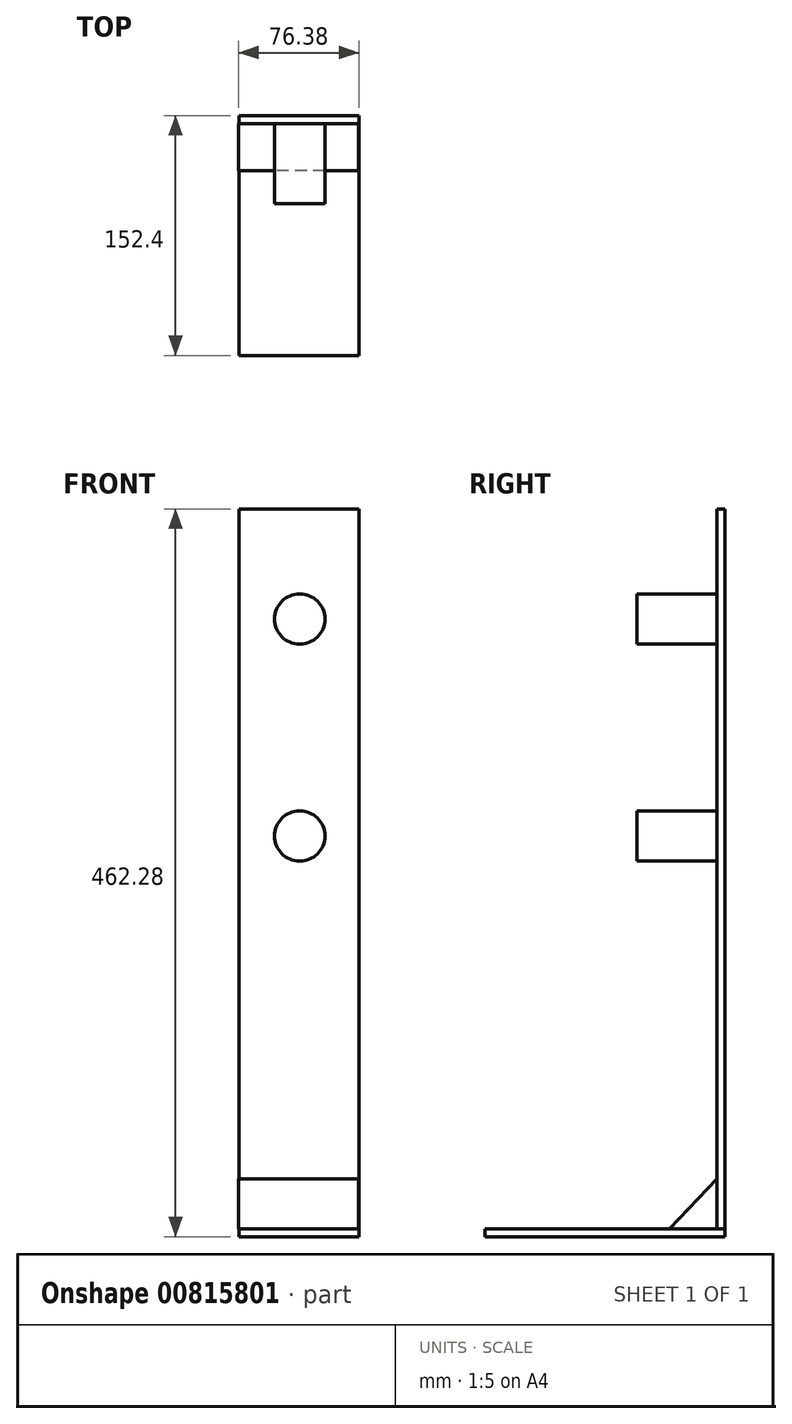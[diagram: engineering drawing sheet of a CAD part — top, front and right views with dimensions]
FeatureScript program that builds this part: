
annotation { "Feature Type Name" : "Feature", "Feature Type Description" : "" }
export const myFeature = defineFeature(function(context is Context, id is Id, definition is map)
    precondition{}
    {
        {
            var Q0;
            Q0=qCreatedBy(makeId("Top.planeOp"),FACE);
            var sketch = newSketch(context, id + "F0", { "sketchPlane" : qUnion([Q0])});
            skLineSegment(sketch, "E0.bottom", {"start": v(-25.22, 0) * mm, "end": v(50.98, 0) * mm});
            skLineSegment(sketch, "E0.top", {"start": v(-25.22, -152.4) * mm, "end": v(50.98, -152.4) * mm});
            skLineSegment(sketch, "E0.left", {"start": v(-25.22, 0) * mm, "end": v(-25.22, -152.4) * mm});
            skLineSegment(sketch, "E0.right", {"start": v(50.98, 0) * mm, "end": v(50.98, -152.4) * mm});
            skSolve(sketch);
        }
        {
            var Q0;
            Q0 = qSketchRegion(id + "F0", true);
            extrude(context, id + "F1", {"entities" : qUnion([Q0]), "depth" : 5.08 * mm, "offsetDistance" : 25.4 * mm});
        }
        {
            var Q0;
            Q0=qCreatedBy(makeId("Front.planeOp"),FACE);
            var sketch = newSketch(context, id + "F2", { "sketchPlane" : qUnion([Q0])});
            skLineSegment(sketch, "E1.bottom", {"start": v(50.98, 5.08) * mm, "end": v(-25.22, 5.08) * mm});
            skLineSegment(sketch, "E1.top", {"start": v(50.98, 462.28) * mm, "end": v(-25.22, 462.28) * mm});
            skLineSegment(sketch, "E1.left", {"start": v(50.98, 5.08) * mm, "end": v(50.98, 462.28) * mm});
            skLineSegment(sketch, "E1.right", {"start": v(-25.22, 5.08) * mm, "end": v(-25.22, 462.28) * mm});
            skPoint(sketch, "E1.middle", {"position": v(-63.32, 233.68) * mm});
            skSolve(sketch);
        }
        {
            var Q0;
            Q0 = qSketchRegion(id + "F2", true);
            extrude(context, id + "F3", {"entities" : qUnion([Q0]), "depth" : 5.08 * mm, "offsetDistance" : 25.4 * mm});
        }
        {
            var Q0;
            Q0=qCreatedBy(makeId("Right.planeOp"),FACE);
            var sketch = newSketch(context, id + "F4", { "sketchPlane" : qUnion([Q0])});
            skLineSegment(sketch, "E2", {"start": v(-5.08, 36.86) * mm, "end": v(-5.08, 5.08) * mm});
            skLineSegment(sketch, "E3", {"start": v(-5.08, 5.08) * mm, "end": v(-35.17, 5.08) * mm});
            skLineSegment(sketch, "E4", {"start": v(-35.17, 5.08) * mm, "end": v(-5.08, 36.86) * mm});
            skSolve(sketch);
        }
        {
            var Q0;
            Q0 = qSketchRegion(id + "F4", true);
            extrude(context, id + "F5", {"entities" : qUnion([Q0]), "depth" : 50.8 * mm, "offsetDistance" : 25.4 * mm, "hasSecondDirection" : true, "secondDirectionOppositeDirection" : true, "secondDirectionDepth" : 25.4 * mm});
        }
        {
            var Q0;
            Q0=makeQuery(id+"F3.opExtrude","CAP_FACE",FACE,{"disambiguationData":[OSD([sQuery(id+"F2.wireOp",EDGE,"E1.bottom"),sQuery(id+"F2.wireOp",EDGE,"E1.top"),sQuery(id+"F2.wireOp",EDGE,"E1.left"),sQuery(id+"F2.wireOp",EDGE,"E1.right")])],"isStart":false});
            var sketch = newSketch(context, id + "F6", { "sketchPlane" : qUnion([Q0])});
            skCircle(sketch, "E5", {"center": v(13.4, 392.31) * mm, "radius": 16 * mm});
            skCircle(sketch, "E6", {"center": v(13.4, 254.52) * mm, "radius": 16 * mm});
            skSolve(sketch);
        }
        {
            var Q0;
            Q0 = qSketchRegion(id + "F6", true);
            extrude(context, id + "F7", {"entities" : qUnion([Q0]), "operationType" : NewBodyOperationType.ADD, "depth" : 50.8 * mm, "offsetDistance" : 25.4 * mm});
        }
    });
